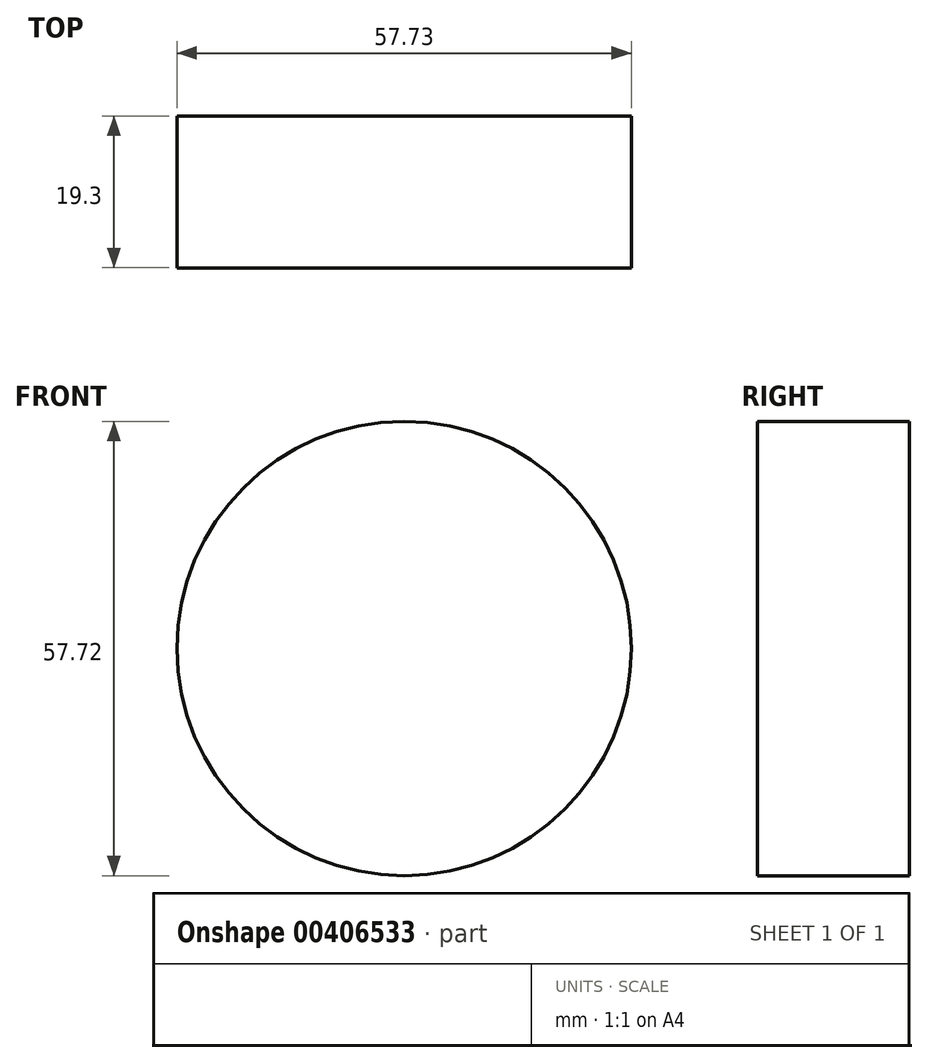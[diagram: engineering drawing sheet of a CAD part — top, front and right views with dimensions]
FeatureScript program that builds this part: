
annotation { "Feature Type Name" : "Feature", "Feature Type Description" : "" }
export const myFeature = defineFeature(function(context is Context, id is Id, definition is map)
    precondition{}
    {
        {
            var Q0;
            Q0=qCreatedBy(makeId("Front.planeOp"),FACE);
            var sketch = newSketch(context, id + "F0", { "sketchPlane" : qUnion([Q0])});
            skLineSegment(sketch, "E0", {"start": v(46.7, 33.88) * mm, "end": v(-29.61, 36.16) * mm});
            skLineSegment(sketch, "E1", {"start": v(-29.61, 36.16) * mm, "end": v(-5.88, 3.32) * mm});
            skCircle(sketch, "E2", {"center": v(36.45, 3.13) * mm, "radius": 28.86 * mm});
            skSolve(sketch);
        }
        {
            var Q0;
            Q0=makeQuery(id+"F0.imprint","IMPRINT",FACE,{"disambiguationData":[TD([[makeQuery(id+"F0.imprint","IMPRINT",EDGE,{"derivedFrom":sQuery(id+"F0.wireOp",EDGE,"E2")}),1.0]])]});
            extrude(context, id + "F1", {"entities" : qUnion([Q0]), "depth" : 19.3 * mm});
        }
    });
